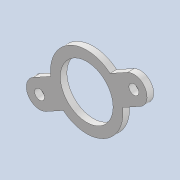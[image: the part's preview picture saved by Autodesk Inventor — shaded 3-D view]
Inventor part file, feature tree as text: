
AUTODESK INVENTOR PART (.ipt)
format: ipt  version: 2020 (Build 240168000, 168)  size: 213,504 bytes
history: native  units: mm
features: other x5, extrude x4, sketch x3, fillet x2, reference x2, projected_geometry x2, plane x1
ambient origin geometry x8: Origin, YZ Plane, XZ Plane, XY Plane, X Axis, Y Axis, Z Axis, Center Point
bodies: Solid1 (feature_tree)
feature tree (19):
  extrude  "Extrusion1"  Depth=8.0mm
  extrude  "Extrusion3"  Depth=2.0mm TaperAngle=0.0deg
  sketch  "Sketch5"  dims[d7=5.2mm d8=5.2mm d9=1.8mm d10=1.8mm d11=2.0mm d12=0.0mm d13=4.0mm d14=2.8mm d15=4.0mm d16=2.8mm d17=2.0mm d18=0.0mm d19=2.0mm d20=0.0mm d21=2.0mm d25=0.5mm]
  extrude  "Extrusion4"  Depth=0.5mm
  plane  "Work Plane1"
  extrude  "Extrusion5"  Depth=0.5mm
  fillet  "Fillet1"  Radius=1.8mm
  fillet  "Fillet2"  Radius=2.0mm
  sketch  "Sketch1"  dims[d0=4.0mm d1=8.0mm]
  reference  "Reference1"
  reference  "Reference2"
  sketch  "Sketch4"  dims[d2=11.0mm d3=2.0mm d4=0.0mm]
  projected_geometry  "Projected Loop2"
  projected_geometry  "Projected Loop3"
  parser-record x1  (decoder bookkeeping rows leaked as tree rows — omitted from the tree; the rows remain in map.json)
  other  "tip_ass_t1.iam"
  other  "pin_conn_1:1"
  other  "motor_1608:1"
  other  "motor_1608_inner:1"
note: 1 file-system path scrubbed to <path> (originals preserved in map.json)
